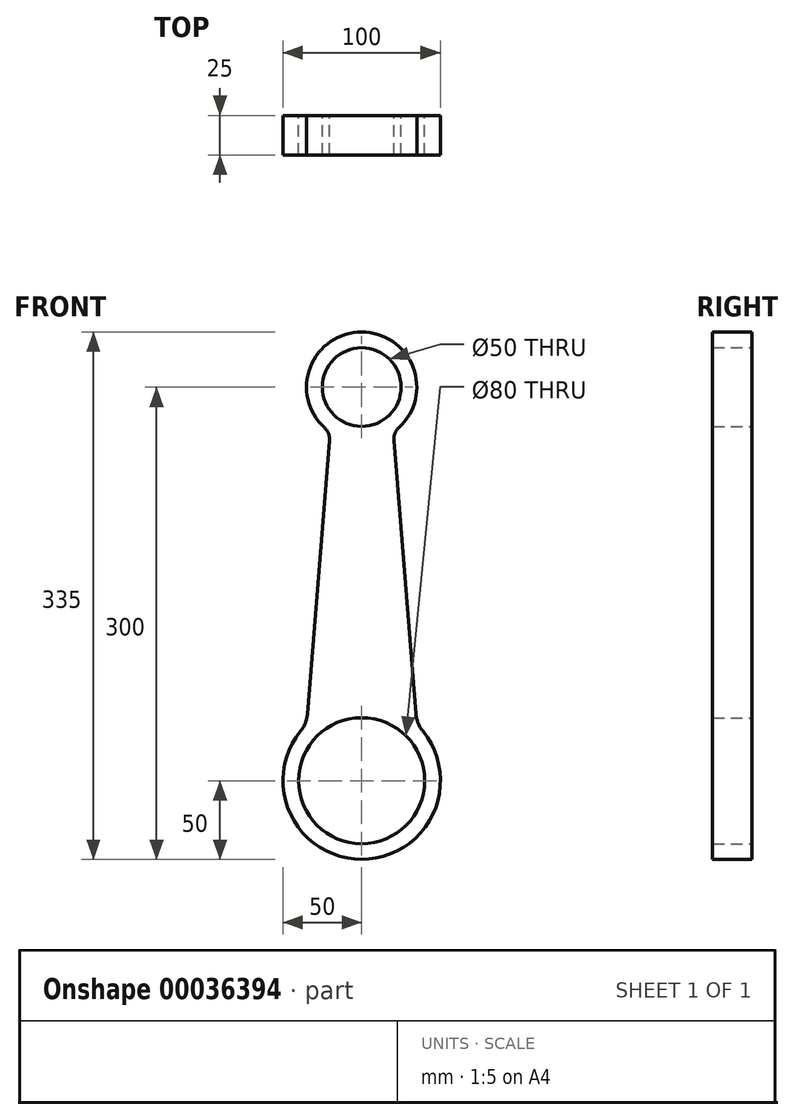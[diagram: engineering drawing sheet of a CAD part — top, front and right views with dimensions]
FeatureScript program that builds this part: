
annotation { "Feature Type Name" : "Feature", "Feature Type Description" : "" }
export const myFeature = defineFeature(function(context is Context, id is Id, definition is map)
    precondition{}
    {
        {
            var Q0;
            Q0=qCreatedBy(makeId("Front.planeOp"),FACE);
            var sketch = newSketch(context, id + "F0", { "sketchPlane" : qUnion([Q0])});
            skArc(sketch, "E0", {"start": v(23.64, 99.19) * mm, "mid": v(0, 160) * mm, "end": v(-23.64, 99.19) * mm});
            skCircle(sketch, "E1", {"center": v(0, 125) * mm, "radius": 25 * mm});
            skArc(sketch, "E2", {"start": v(-38.85, -93.52) * mm, "mid": v(0, -175) * mm, "end": v(38.85, -93.52) * mm});
            skCircle(sketch, "E3", {"center": v(0, -125) * mm, "radius": 40 * mm});
            skLineSegment(sketch, "E4", {"start": v(-34.45, -82.55) * mm, "end": v(-20.43, 91) * mm});
            skLineSegment(sketch, "E5", {"start": v(34.45, -82.55) * mm, "end": v(20.43, 91) * mm});
            skPoint(sketch, "E6.visualSharp", {"position": v(-20, 96.28) * mm});
            skArc(sketch, "E6.filletArc", {"start": v(-20.43, 91) * mm, "mid": v(-21.09, 95.47) * mm, "end": v(-23.64, 99.19) * mm});
            skPoint(sketch, "E7.visualSharp", {"position": v(20, 96.28) * mm});
            skArc(sketch, "E7.filletArc", {"start": v(23.64, 99.19) * mm, "mid": v(21.09, 95.47) * mm, "end": v(20.43, 91) * mm});
            skPoint(sketch, "E8.visualSharp", {"position": v(-35, -89.3) * mm});
            skArc(sketch, "E8.filletArc", {"start": v(-38.85, -93.52) * mm, "mid": v(-35.82, -88.37) * mm, "end": v(-34.45, -82.55) * mm});
            skPoint(sketch, "E9.visualSharp", {"position": v(35, -89.3) * mm});
            skArc(sketch, "E9.filletArc", {"start": v(34.45, -82.55) * mm, "mid": v(35.82, -88.37) * mm, "end": v(38.85, -93.52) * mm});
            skSolve(sketch);
        }
        {
            var Q0;
            Q0=makeQuery(id+"F0.imprint","IMPRINT",FACE,{"disambiguationData":[TD([[makeQuery(id+"F0.imprint","IMPRINT",EDGE,{"derivedFrom":sQuery(id+"F0.wireOp",EDGE,"E0")}),1.0]])]});
            extrude(context, id + "F1", {"entities" : qUnion([Q0]), "depth" : 25 * mm});
        }
    });
